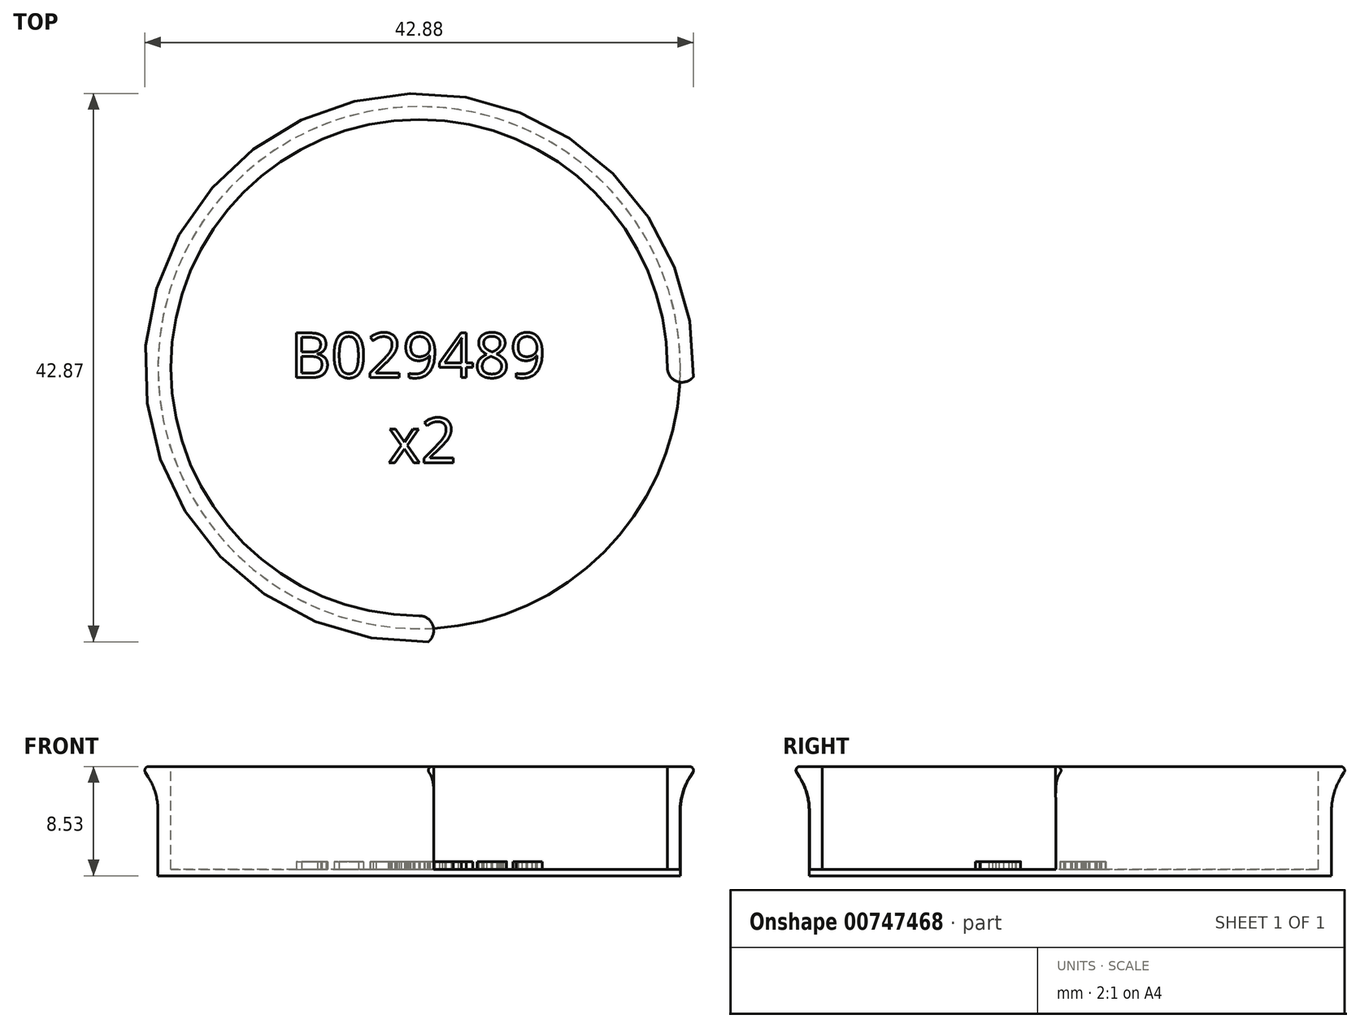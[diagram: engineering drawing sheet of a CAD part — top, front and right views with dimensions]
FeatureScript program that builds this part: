
annotation { "Feature Type Name" : "Feature", "Feature Type Description" : "" }
export const myFeature = defineFeature(function(context is Context, id is Id, definition is map)
    precondition{}
    {
        {
            var Q0;
            Q0=qCreatedBy(makeId("Right.planeOp"),FACE);
            var sketch = newSketch(context, id + "F0", { "sketchPlane" : qUnion([Q0])});
            skLineSegment(sketch, "E0", {"start": v(5.75, 8.53) * mm, "end": v(5.75, 0) * mm});
            skLineSegment(sketch, "E1", {"start": v(5.75, 8.53) * mm, "end": v(-15.93, 8.53) * mm});
            skLineSegment(sketch, "E2", {"start": v(5.75, 0) * mm, "end": v(-14.66, 0) * mm});
            skLineSegment(sketch, "E3", {"start": v(-14.66, 0) * mm, "end": v(-14.66, 6.5) * mm});
            skLineSegment(sketch, "E4", {"start": v(-14.66, 6.5) * mm, "end": v(-14.66, 8.53) * mm});
            skLineSegment(sketch, "E5", {"start": v(-15.93, 8.53) * mm, "end": v(-14.66, 6.5) * mm});
            skSolve(sketch);
        }
        {
            var Q0;
            Q0=qSketchRegion(id+"F0",true);
            var Q1;
            Q1=sQuery(id+"F0.wireOp",EDGE,"E0");
            revolve(context, id + "F1", {"entities" : qUnion([Q0]), "axis" : qUnion([Q1]), "revolveType" : RevolveType.FULL});
        }
        {
            var Q0;
            Q0=makeQuery(id+"F1.opRevolve","SWEPT_FACE",FACE,{"disambiguationData":[OSD([sQuery(id+"F0.wireOp",EDGE,"E1")])]});
            var sketch = newSketch(context, id + "F2", { "sketchPlane" : qUnion([Q0])});
            skCircle(sketch, "E6", {"center": v(0, 5.75) * mm, "radius": 19.4 * mm});
            skLineSegment(sketch, "E7.bottom", {"start": v(0, 5.75) * mm, "end": v(21.68, 5.75) * mm});
            skLineSegment(sketch, "E7.top", {"start": v(0, -15.93) * mm, "end": v(21.68, -15.93) * mm});
            skLineSegment(sketch, "E7.left", {"start": v(0, 5.75) * mm, "end": v(0, -15.93) * mm});
            skLineSegment(sketch, "E7.right", {"start": v(21.68, 5.75) * mm, "end": v(21.68, -15.93) * mm});
            skArc(sketch, "E8", {"start": v(0, -15.93) * mm, "mid": v(1.14, -14.78) * mm, "end": v(0, -13.64) * mm});
            skArc(sketch, "E9", {"start": v(19.4, 5.75) * mm, "mid": v(20.54, 4.61) * mm, "end": v(21.68, 5.75) * mm});
            skSolve(sketch);
        }
        {
            var Q0;
            {var subQ0=sQuery(id+"F2.wireOp",EDGE,"E7.left");var subQ3=sQuery(id+"F2.wireOp",EDGE,"E7.bottom");var subQ5=makeQuery(id+"F2.imprint","INTERSECT",VERTEX,{"derivedFrom":[subQ3,subQ0]});Q0=makeQuery(id+"F2.imprint","IMPRINT",FACE,{"disambiguationData":[TD([[makeQuery(id+"F2.imprint","IMPRINT",EDGE,{"disambiguationData":[TD([[subQ5,-1.0]])],"derivedFrom":subQ3}),1.0]])]});}
            var Q1;
            {var subQ0=sQuery(id+"F2.wireOp",EDGE,"E7.left");var subQ3=sQuery(id+"F2.wireOp",EDGE,"E7.bottom");var subQ5=makeQuery(id+"F2.imprint","INTERSECT",VERTEX,{"derivedFrom":[subQ3,subQ0]});Q1=makeQuery(id+"F2.imprint","IMPRINT",FACE,{"disambiguationData":[TD([[makeQuery(id+"F2.imprint","IMPRINT",EDGE,{"disambiguationData":[TD([[subQ5,-1.0]])],"derivedFrom":subQ3}),-1.0]])]});}
            var Q2;
            {var subQ0=sQuery(id+"F2.wireOp",EDGE,"E8");Q2=makeQuery(id+"F2.imprint","IMPRINT",FACE,{"disambiguationData":[TD([[makeQuery(id+"F2.imprint","IMPRINT",EDGE,{"derivedFrom":subQ0}),-1.0]])]});}
            extrude(context, id + "F3", {"entities" : qUnion([Q0, Q1, Q2]), "operationType" : NewBodyOperationType.REMOVE, "oppositeDirection" : true, "depth" : 8.03 * mm});
        }
        {
            var Q0;
            Q0=makeQuery(id+"F1.opRevolve","SWEPT_EDGE",EDGE,{"disambiguationData":[OSD([sQuery(id+"F0.wireOp",EDGE,"E1"),sQuery(id+"F0.wireOp",EDGE,"E5")])]});
            var Q1;
            Q1=makeQuery(id+"F3.boolean.opBoolean","COPY",EDGE,{"derivedFrom":makeQuery(id+"F3.opExtrude","CAP_EDGE",EDGE,{"disambiguationData":[OSD([sQuery(id+"F2.wireOp",EDGE,"E6")])],"isStart":true})});
            fillet(context, id + "F4", {"entities" : qUnion([Q0, Q1]), "radius" : 0.3 * mm, "tangentPropagation" : true, "allowEdgeOverflow" : false});
        }
        {
            var Q0;
            Q0=makeQuery(id+"F1.opRevolve","SWEPT_EDGE",EDGE,{"disambiguationData":[OSD([sQuery(id+"F0.wireOp",EDGE,"E3"),sQuery(id+"F0.wireOp",EDGE,"E4"),sQuery(id+"F0.wireOp",EDGE,"E5")])]});
            fillet(context, id + "F5", {"entities" : qUnion([Q0]), "radius" : 5 * mm, "tangentPropagation" : true, "allowEdgeOverflow" : false});
        }
        {
            var Q0;
            Q0=makeQuery(id+"F3.boolean.opBoolean","COPY",FACE,{"derivedFrom":makeQuery(id+"F3.opExtrude","CAP_FACE",FACE,{"disambiguationData":[OSD([sQuery(id+"F0.wireOp",EDGE,"E1"),sQuery(id+"F0.wireOp",EDGE,"E5"),sQuery(id+"F2.wireOp",EDGE,"E6"),sQuery(id+"F2.wireOp",EDGE,"E8"),sQuery(id+"F2.wireOp",EDGE,"E9")])],"isStart":false})});
            var sketch = newSketch(context, id + "F6", { "sketchPlane" : qUnion([Q0])});
            skText(sketch, "E10", { "text": "B029489\n      x2", "fontName": "OpenSans-Regular.ttf"});
            const initialGuessF6  = {"E10": [-0.01006, 0.00498, 1, 0, 0.00352]};
            skSetInitialGuess(sketch, initialGuessF6);
            skSolve(sketch);
        }
        {
            var Q0;
            Q0=qSketchRegion(id+"F6",true);
            extrude(context, id + "F7", {"entities" : qUnion([Q0]), "operationType" : NewBodyOperationType.ADD, "depth" : 0.6 * mm, "offsetDistance" : 25 * mm});
        }
    });
